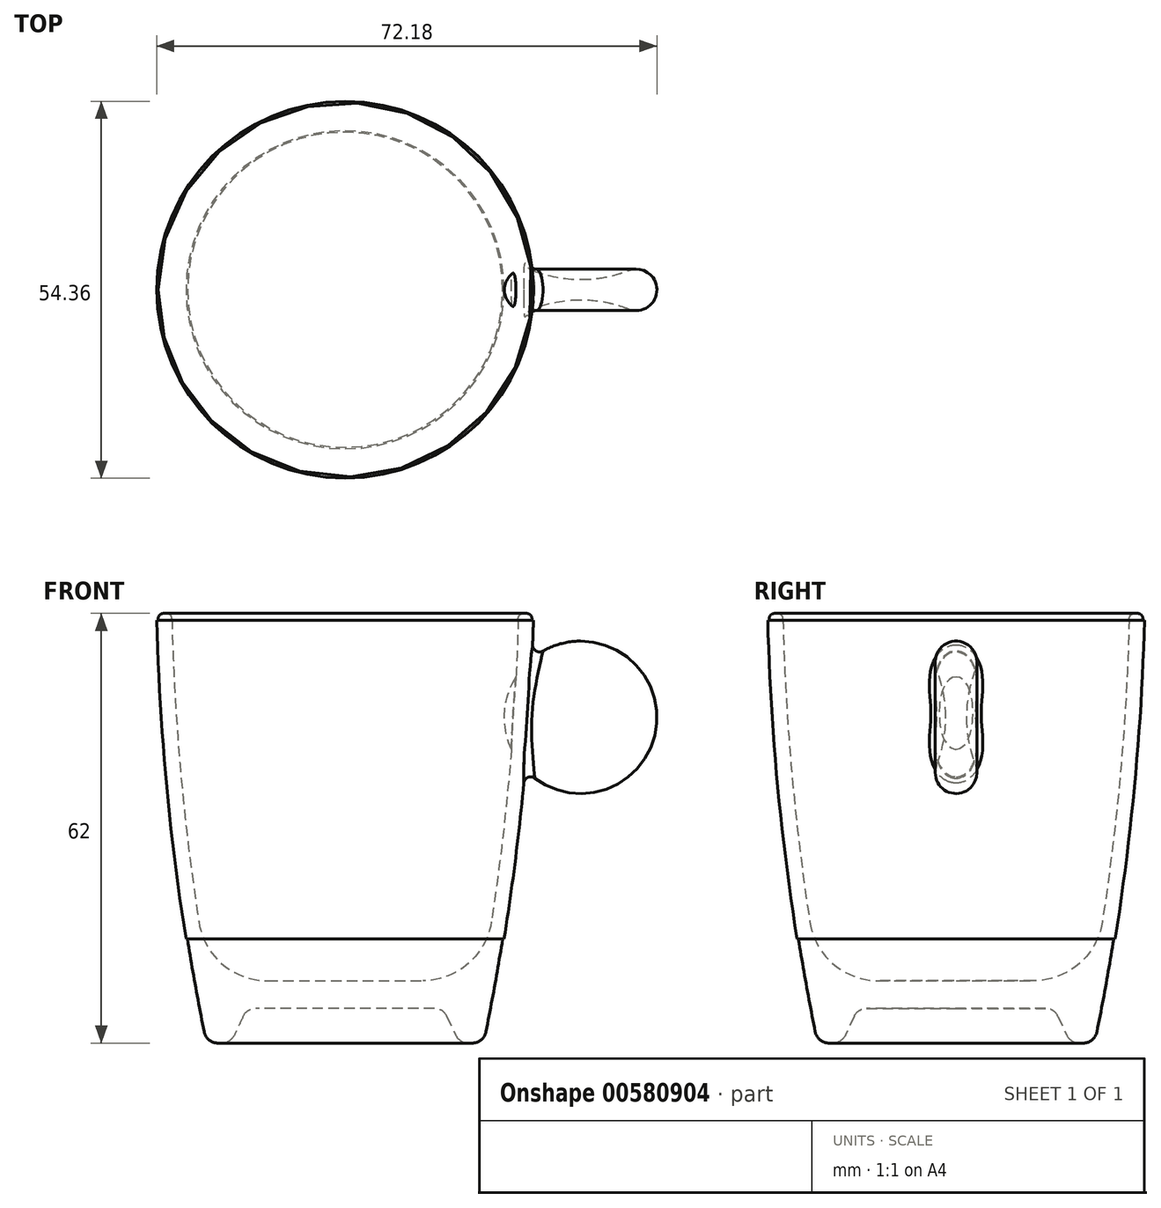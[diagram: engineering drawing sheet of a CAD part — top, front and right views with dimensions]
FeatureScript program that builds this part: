
annotation { "Feature Type Name" : "Feature", "Feature Type Description" : "" }
export const myFeature = defineFeature(function(context is Context, id is Id, definition is map)
    precondition{}
    {
        {
            var Q0;
            Q0=qCreatedBy(makeId("Front.planeOp"),FACE);
            var sketch = newSketch(context, id + "F0", { "sketchPlane" : qUnion([Q0])});
            skLineSegment(sketch, "E0", {"start": v(0, 5) * mm, "end": v(14.17, 5) * mm});
            skLineSegment(sketch, "E1", {"start": v(14.17, 5) * mm, "end": v(16.5, 0) * mm});
            skLineSegment(sketch, "E2", {"start": v(16.5, 0) * mm, "end": v(20, 0) * mm});
            skArc(sketch, "E3", {"start": v(20, 0) * mm, "mid": v(24.9, 30.84) * mm, "end": v(27, 62) * mm});
            skLineSegment(sketch, "E4", {"start": v(27, 62) * mm, "end": v(25, 62) * mm});
            skLineSegment(sketch, "E5", {"start": v(0, 9) * mm, "end": v(0, 5) * mm});
            skLineSegment(sketch, "E6", {"start": v(19.7, 9) * mm, "end": v(0, 9) * mm});
            skArc(sketch, "E7.trimOffspring", {"start": v(19.7, 9) * mm, "mid": v(23.38, 35.4) * mm, "end": v(25, 62) * mm});
            skPoint(sketch, "E8.orphan", {"position": v(0, 62) * mm});
            skSolve(sketch);
        }
        {
            var Q0;
            Q0=qSketchRegion(id+"F0",true);
            var Q1;
            Q1=sQuery(id+"F0.wireOp",EDGE,"E5");
            revolve(context, id + "F1", {"entities" : qUnion([Q0]), "axis" : qUnion([Q1]), "revolveType" : RevolveType.FULL});
        }
        {
            var Q0;
            Q0=makeQuery(id+"F1.opRevolve","SWEPT_EDGE",EDGE,{"disambiguationData":[OSD([sQuery(id+"F0.wireOp",EDGE,"E4"),sQuery(id+"F0.wireOp",EDGE,"E7.trimOffspring")])]});
            var Q1;
            Q1=makeQuery(id+"F1.opRevolve","SWEPT_EDGE",EDGE,{"disambiguationData":[OSD([sQuery(id+"F0.wireOp",EDGE,"E3"),sQuery(id+"F0.wireOp",EDGE,"E4")])]});
            fillet(context, id + "F2", {"entities" : qUnion([Q0, Q1]), "radius" : .8 * mm, "tangentPropagation" : true, "allowEdgeOverflow" : false});
        }
        {
            var Q0;
            Q0=makeQuery(id+"F1.opRevolve","SWEPT_EDGE",EDGE,{"disambiguationData":[OSD([sQuery(id+"F0.wireOp",EDGE,"E2"),sQuery(id+"F0.wireOp",EDGE,"E3")])]});
            var Q1;
            Q1=makeQuery(id+"F1.opRevolve","SWEPT_EDGE",EDGE,{"disambiguationData":[OSD([sQuery(id+"F0.wireOp",EDGE,"E1"),sQuery(id+"F0.wireOp",EDGE,"E2")])]});
            var Q2;
            Q2=makeQuery(id+"F1.opRevolve","SWEPT_EDGE",EDGE,{"disambiguationData":[OSD([sQuery(id+"F0.wireOp",EDGE,"E0"),sQuery(id+"F0.wireOp",EDGE,"E1")])]});
            fillet(context, id + "F3", {"entities" : qUnion([Q0, Q1, Q2]), "radius" : 2 * mm, "tangentPropagation" : true, "allowEdgeOverflow" : false});
        }
        {
            var Q0;
            Q0=makeQuery(id+"F1.opRevolve","SWEPT_EDGE",EDGE,{"disambiguationData":[OSD([sQuery(id+"F0.wireOp",EDGE,"E6"),sQuery(id+"F0.wireOp",EDGE,"E7.trimOffspring")])]});
            fillet(context, id + "F4", {"entities" : qUnion([Q0]), "radius" : 10 * mm, "tangentPropagation" : true, "allowEdgeOverflow" : false});
        }
        {
            var Q0;
            Q0=qCreatedBy(makeId("Front.planeOp"),FACE);
            var sketch = newSketch(context, id + "F5", { "sketchPlane" : qUnion([Q0])});
            skArc(sketch, "E9", {"start": v(22.74, 15) * mm, "mid": v(25.63, 37.93) * mm, "end": v(26.98, 61) * mm});
            skLineSegment(sketch, "E10", {"start": v(26.98, 61) * mm, "end": v(27.18, 61) * mm});
            skLineSegment(sketch, "E11", {"start": v(22.74, 15) * mm, "end": v(22.94, 15) * mm});
            skArc(sketch, "E12", {"start": v(22.94, 15) * mm, "mid": v(25.83, 37.93) * mm, "end": v(27.18, 61) * mm});
            skSolve(sketch);
        }
        {
            var Q0;
            Q0=makeQuery(id+"F5.imprint","IMPRINT",FACE,{"disambiguationData":[TD([[makeQuery(id+"F5.imprint","IMPRINT",EDGE,{"derivedFrom":sQuery(id+"F5.wireOp",EDGE,"E9")}),-1.0]])]});
            var Q1;
            Q1=sQuery(id+"F0.wireOp",EDGE,"E5");
            revolve(context, id + "F6", {"operationType" : NewBodyOperationType.ADD, "entities" : qUnion([Q0]), "axis" : qUnion([Q1]), "revolveType" : RevolveType.FULL});
        }
        {
            var Q0;
            Q0=makeQuery(id+"F1.opRevolve","SWEPT_FACE",FACE,{"disambiguationData":[OSD([sQuery(id+"F0.wireOp",EDGE,"E4")])]});
            cPlane(context, id + "F7", {"entities" : qUnion([Q0]), "cplaneType" : CPlaneType.OFFSET, "offset" : 15 * mm, "oppositeDirection" : true, "width" : 150 * mm, "height" : 150 * mm});
        }
        {
            var Q0;
            Q0=qCreatedBy(id+"F7.planeOp",FACE);
            var sketch = newSketch(context, id + "F8", { "sketchPlane" : qUnion([Q0])});
            skArc(sketch, "E13", {"start": v(45, 0) * mm, "mid": v(43.7, 2.48) * mm, "end": v(40.91, 2.8) * mm});
            skArc(sketch, "E14", {"start": v(34, 1.5) * mm, "mid": v(37.52, 1.83) * mm, "end": v(40.91, 2.8) * mm});
            skLineSegment(sketch, "E15", {"start": v(34, 1.5) * mm, "end": v(34, 0) * mm});
            skLineSegment(sketch, "E16.MirrorCS", {"start": v(34, -1.5) * mm, "end": v(34, 0) * mm});
            skArc(sketch, "E17.MirrorCS", {"start": v(34, -1.5) * mm, "mid": v(37.52, -1.83) * mm, "end": v(40.91, -2.8) * mm});
            skArc(sketch, "E18.MirrorCS", {"start": v(45, 0) * mm, "mid": v(43.7, -2.48) * mm, "end": v(40.91, -2.8) * mm});
            skSolve(sketch);
        }
        {
            var Q0;
            Q0=makeQuery(id+"F8.imprint","IMPRINT",FACE,{"disambiguationData":[TD([[makeQuery(id+"F8.imprint","IMPRINT",EDGE,{"derivedFrom":sQuery(id+"F8.wireOp",EDGE,"E13")}),1.0]])]});
            var Q1;
            Q1=sQuery(id+"F8.wireOp",EDGE,"E15");
            revolve(context, id + "F9", {"operationType" : NewBodyOperationType.ADD, "entities" : qUnion([Q0]), "axis" : qUnion([Q1]), "revolveType" : RevolveType.FULL});
        }
        {
            var Q0;
            Q0=makeQuery(id+"F9.boolean.opBoolean","INTERSECT",EDGE,{"derivedFrom":[makeQuery(id+"F6.opRevolve","SWEPT_FACE",FACE,{"disambiguationData":[OSD([sQuery(id+"F5.wireOp",EDGE,"E12")])]}),makeQuery(id+"F9.opRevolve","SWEPT_FACE",FACE,{"disambiguationData":[OSD([sQuery(id+"F8.wireOp",EDGE,"E13"),sQuery(id+"F8.wireOp",EDGE,"E18.MirrorCS")])]})]});
            fillet(context, id + "F10", {"entities" : qUnion([Q0]), "radius" : 1 * mm, "tangentPropagation" : true, "allowEdgeOverflow" : false});
        }
    });
